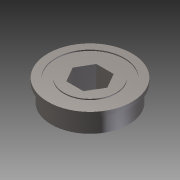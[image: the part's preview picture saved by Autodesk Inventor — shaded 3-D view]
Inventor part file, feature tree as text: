
AUTODESK INVENTOR PART (.ipt)
format: ipt  version: 2015 SP1 (Build 190203100, 203)  size: 177,664 bytes
history: native  units: in
note: dims shown in document units (in); Inventor stores cm internally (conversion verified against a paired STEP export)
features: other x2, extrude x1, imported_body x1, sketch x1, projected_geometry x1
ambient origin geometry x8: Origin, YZ Plane, XZ Plane, XY Plane, X Axis, Y Axis, Z Axis, Center Point
bodies: Body1 (feature_tree)
feature tree (6):
  other  "Cut-Extrude1"
  other  "0.5 hex bearing1"
  extrude  "Extrusion1"  Depth=0.4375in
  imported_body  "Base1"
  sketch  "Sketch1"  dims[d0=0.4375in d1=0.4375in d2=0.4375in d3=120.0deg d4=120.0deg d5=0.2188in d6=0.2188in d7=0.2188in d8=0.3125in d9=0.0in]
  projected_geometry  "Projected Loop1"
